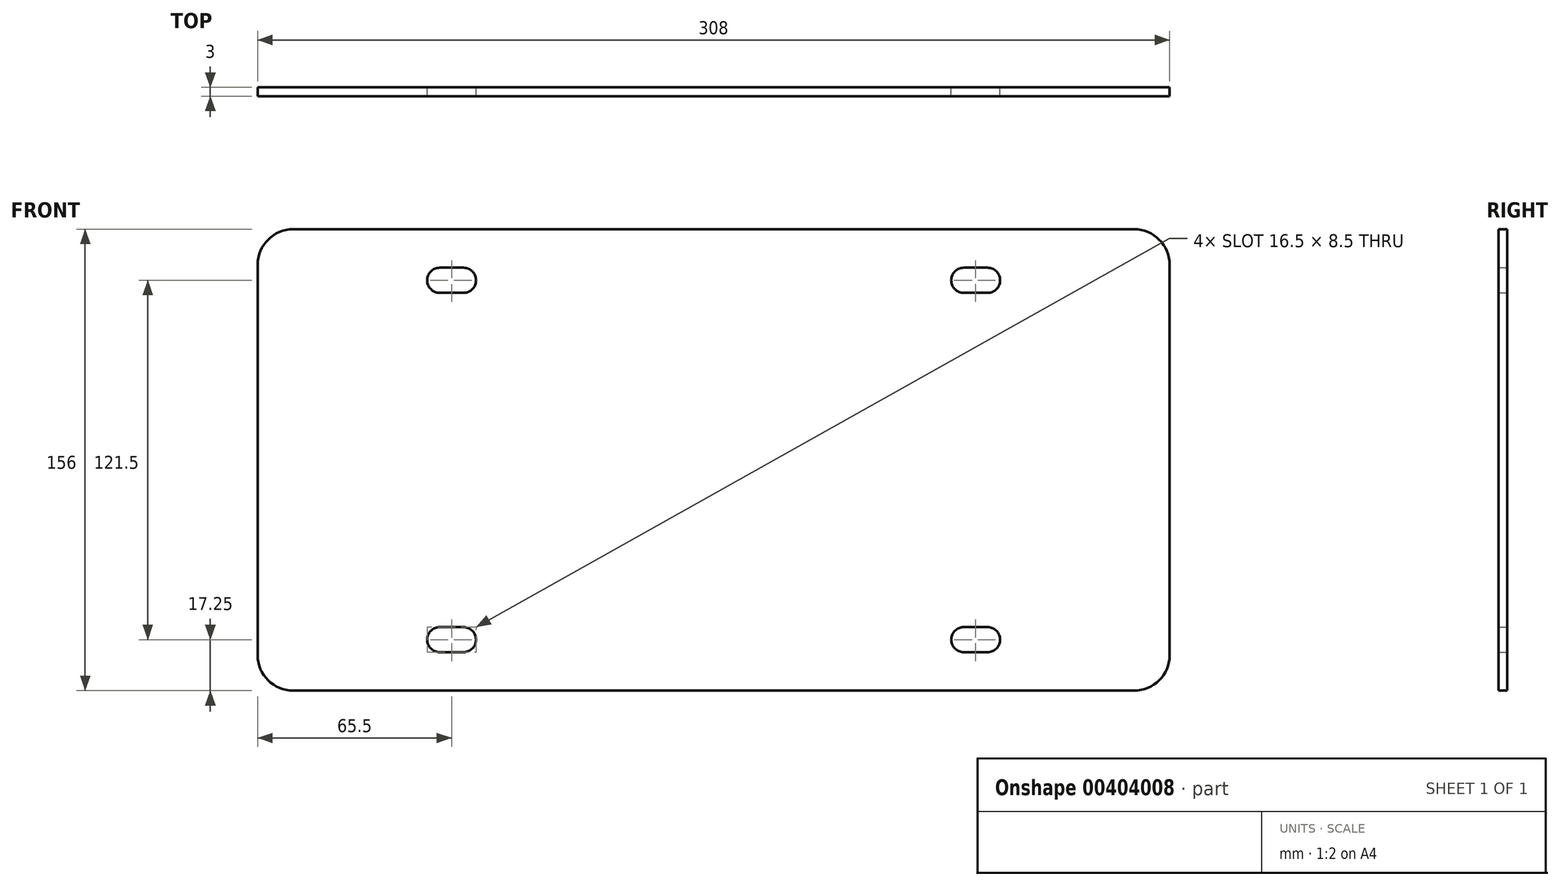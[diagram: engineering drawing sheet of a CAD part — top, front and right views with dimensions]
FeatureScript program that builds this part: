
annotation { "Feature Type Name" : "Feature", "Feature Type Description" : "" }
export const myFeature = defineFeature(function(context is Context, id is Id, definition is map)
    precondition{}
    {
        {
            var Q0;
            Q0=qCreatedBy(makeId("Front.planeOp"),FACE);
            var sketch = newSketch(context, id + "F0", { "sketchPlane" : qUnion([Q0])});
            skLineSegment(sketch, "E0.bottom", {"start": v(142, 78) * mm, "end": v(-142, 78) * mm});
            skLineSegment(sketch, "E0.top", {"start": v(142, -78) * mm, "end": v(-142, -78) * mm});
            skLineSegment(sketch, "E0.left", {"start": v(154, 66) * mm, "end": v(154, -66) * mm});
            skLineSegment(sketch, "E0.right", {"start": v(-154, 66) * mm, "end": v(-154, -66) * mm});
            skPoint(sketch, "E0.middle", {"position": v(0, 0) * mm});
            skPoint(sketch, "E1.visualSharp", {"position": v(-154, 78) * mm});
            skArc(sketch, "E1.filletArc", {"start": v(-142, 78) * mm, "mid": v(-150.49, 74.49) * mm, "end": v(-154, 66) * mm});
            skPoint(sketch, "E2.visualSharp", {"position": v(-154, -78) * mm});
            skArc(sketch, "E2.filletArc", {"start": v(-154, -66) * mm, "mid": v(-150.49, -74.49) * mm, "end": v(-142, -78) * mm});
            skPoint(sketch, "E3.visualSharp", {"position": v(154, 78) * mm});
            skArc(sketch, "E3.filletArc", {"start": v(154, 66) * mm, "mid": v(150.49, 74.49) * mm, "end": v(142, 78) * mm});
            skPoint(sketch, "E4.visualSharp", {"position": v(154, -78) * mm});
            skArc(sketch, "E4.filletArc", {"start": v(142, -78) * mm, "mid": v(150.49, -74.49) * mm, "end": v(154, -66) * mm});
            skLineSegment(sketch, "E5", {"start": v(-92.5, 60.75) * mm, "end": v(-84.5, 60.75) * mm});
            skLineSegment(sketch, "E6", {"start": v(-88.5, 60.75) * mm, "end": v(-88.5, 46.04) * mm, "construction": true});
            skArc(sketch, "E7.0.startCap", {"start": v(-92.5, 56.5) * mm, "mid": v(-96.75, 60.75) * mm, "end": v(-92.5, 65) * mm});
            skArc(sketch, "E7.0.endCap", {"start": v(-84.5, 65) * mm, "mid": v(-80.25, 60.75) * mm, "end": v(-84.5, 56.5) * mm});
            skLineSegment(sketch, "E7.0.left", {"start": v(-92.5, 65) * mm, "end": v(-84.5, 65) * mm});
            skLineSegment(sketch, "E7.0.right", {"start": v(-92.5, 56.5) * mm, "end": v(-84.5, 56.5) * mm});
            skLineSegment(sketch, "E8", {"start": v(0, 0) * mm, "end": v(0, 50.5) * mm, "construction": true});
            skLineSegment(sketch, "E9", {"start": v(0, 0) * mm, "end": v(-92.14, 0) * mm, "construction": true});
            skLineSegment(sketch, "E10.MirrorCS", {"start": v(92.5, 65) * mm, "end": v(84.5, 65) * mm});
            skArc(sketch, "E11.MirrorCS", {"start": v(92.5, 56.5) * mm, "mid": v(96.75, 60.75) * mm, "end": v(92.5, 65) * mm});
            skLineSegment(sketch, "E12.MirrorCS", {"start": v(92.5, 56.5) * mm, "end": v(84.5, 56.5) * mm});
            skArc(sketch, "E13.MirrorCS", {"start": v(84.5, 65) * mm, "mid": v(80.25, 60.75) * mm, "end": v(84.5, 56.5) * mm});
            skArc(sketch, "E14.MirrorCS", {"start": v(-84.5, -65) * mm, "mid": v(-80.25, -60.75) * mm, "end": v(-84.5, -56.5) * mm});
            skLineSegment(sketch, "E15.MirrorCS", {"start": v(-92.5, -65) * mm, "end": v(-84.5, -65) * mm});
            skArc(sketch, "E16.MirrorCS", {"start": v(-92.5, -56.5) * mm, "mid": v(-96.75, -60.75) * mm, "end": v(-92.5, -65) * mm});
            skLineSegment(sketch, "E17.MirrorCS", {"start": v(-92.5, -56.5) * mm, "end": v(-84.5, -56.5) * mm});
            skLineSegment(sketch, "E18.MirrorCS", {"start": v(92.5, -56.5) * mm, "end": v(84.5, -56.5) * mm});
            skArc(sketch, "E19.MirrorCS", {"start": v(84.5, -65) * mm, "mid": v(80.25, -60.75) * mm, "end": v(84.5, -56.5) * mm});
            skArc(sketch, "E20.MirrorCS", {"start": v(92.5, -56.5) * mm, "mid": v(96.75, -60.75) * mm, "end": v(92.5, -65) * mm});
            skLineSegment(sketch, "E21.MirrorCS", {"start": v(92.5, -65) * mm, "end": v(84.5, -65) * mm});
            skSolve(sketch);
        }
        {
            var Q0;
            Q0 = qSketchRegion(id + "F0", true);
            extrude(context, id + "F1", {"entities" : qUnion([Q0]), "depth" : 3 * mm, "offsetDistance" : 25 * mm});
        }
    });
